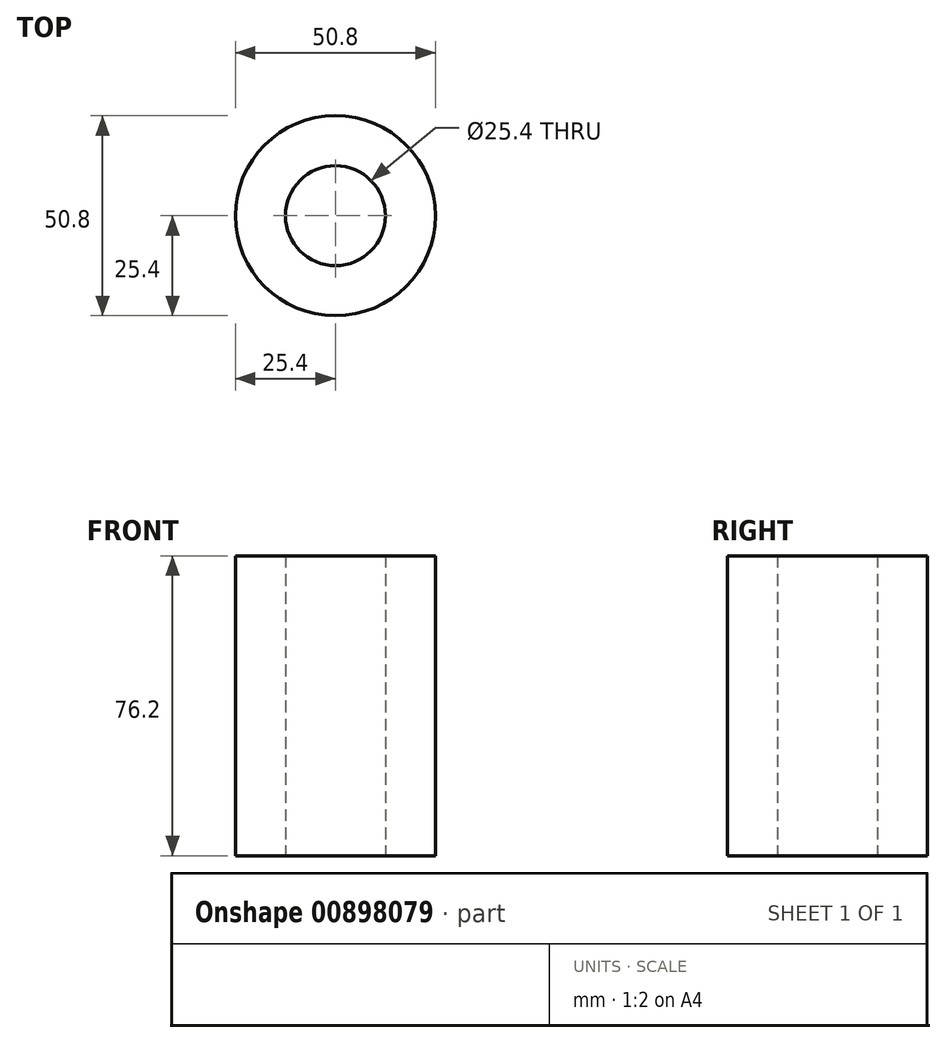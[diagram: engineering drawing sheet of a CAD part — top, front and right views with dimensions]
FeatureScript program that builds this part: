
annotation { "Feature Type Name" : "Feature", "Feature Type Description" : "" }
export const myFeature = defineFeature(function(context is Context, id is Id, definition is map)
    precondition{}
    {
        {
            var Q0;
            Q0=qCreatedBy(makeId("Top.planeOp"),FACE);
            var sketch = newSketch(context, id + "F0", { "sketchPlane" : qUnion([Q0])});
            skCircle(sketch, "E0", {"center": v(0, 0) * mm, "radius": 25.4 * mm});
            skSolve(sketch);
        }
        {
            var Q0;
            Q0 = qSketchRegion(id + "F0", true);
            extrude(context, id + "F1", {"entities" : qUnion([Q0]), "depth" : 76.2 * mm, "offsetDistance" : 25.4 * mm});
        }
        {
            var Q0;
            Q0=makeQuery(id+"F1.opExtrude","CAP_FACE",FACE,{"disambiguationData":[OSD([sQuery(id+"F0.wireOp",EDGE,"E0")])],"isStart":true});
            var sketch = newSketch(context, id + "F2", { "sketchPlane" : qUnion([Q0])});
            skCircle(sketch, "E1", {"center": v(0, 0) * mm, "radius": 12.7 * mm});
            skSolve(sketch);
        }
        {
            var Q0;
            Q0=makeQuery(id+"F2.imprint","IMPRINT",FACE,{"disambiguationData":[TD([[makeQuery(id+"F2.imprint","IMPRINT",EDGE,{"derivedFrom":sQuery(id+"F2.wireOp",EDGE,"E1")}),1.0]])]});
            extrude(context, id + "F3", {"entities" : qUnion([Q0]), "operationType" : NewBodyOperationType.REMOVE, "endBound" : BoundingType.THROUGH_ALL, "oppositeDirection" : true, "depth" : 25.4 * mm, "offsetDistance" : 25.4 * mm});
        }
    });
